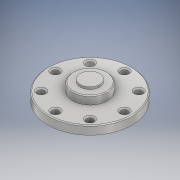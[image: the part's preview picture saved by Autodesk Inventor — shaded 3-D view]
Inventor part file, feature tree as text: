
AUTODESK INVENTOR PART (.ipt)
format: ipt  version: 2023 (Build 270158000, 158)  size: 413,696 bytes
history: native  units: mm
features: other x3, extrude x3, sketch x3
ambient origin geometry x8: Origin, YZ Plane, XZ Plane, XY Plane, X Axis, Y Axis, Z Axis, Center Point
bodies: Body1 (feature_tree)
feature tree (9):
  other  "ソリッド1"
  other  "作業平面1"
  extrude  "押し出し1"  Depth=0.5mm
  extrude  "押し出し2"  Depth=10.0mm TaperAngle=0.0deg
  extrude  "押し出し3"  Depth=15.0mm
  sketch  "スケッチ1"
  sketch  "スケッチ2"
  sketch  "スケッチ3"
  other  "X-430_IDLE_10:1"
